# Revit family: Remeha E-HP AW 168 Plus - Rev A
name_source: partatom
category: Mechanical Equipment
units: mm (PartAtom-declared; Revit-internal decimal feet)

## family parameters
Always vertical = Yes
Cut with Voids When Loaded = No
OmniClass Number = 23.75.00.00
OmniClass Title = Climate Control (HVAC)
Part Type = Normal
Room Calculation Point = No
Round Connector Dimension = Use Diameter
Shared = No
Work Plane-Based = No

## types (1)
- Remeha E-HP AW 168 Plus
    6 Monthly = 05-31
    Access Clearance Bottom = 0 mm  [stored 0 ft]
    Access Clearance Front = 2000 mm  [stored 6.56168 ft]
    Access Clearance Left = 3000 mm  [stored 9.84252 ft]
    Access Clearance Rear = 2000 mm  [stored 6.56168 ft]
    Access Clearance Right = 3000 mm  [stored 9.84252 ft]
    Access Clearance Top = 0 mm  [stored 0 ft]
    Annually = 05-31
    BMS Links = Yes
    Bespoke Timeframe = 0
    CE Mark = Yes
    Coefficient of Performance = 5.16
    Colour = IGP Dura Pol (Brand Colour)
    Condensate Drain Size = 0 mm  [stored 0 ft]
    Configuration = Single unit
    Control Options = Modulating
    Control Type = Weather Compensation, 0-10V, Time Control, DHW Control.
    Daily = 0
    Default Elevation = 0 mm  [stored 0 ft]
    Drain Connection Size = 70 mm  [stored 0.229659 ft]
    Drain Connection Type = Threaded
    Embodied Carbon = 0
    ErP Energy Label = 0
    Expected Life = 0
    External Material = Steel
    Features = The Remeha E-HP AW can be used in projects ranging from small light commercial properties to multi-valent energy centres for large commercial buildings
    Finish = Galvanised & Powder Coated
    Flow and Return Connection Size = 65 mm
    Flow and Return Connection Type = Threaded
    Frequency = 50 Hz
    Full Load Current = 121 A
    Fuse Rating = 0 A
    Global Warming Potential of Refrigerant = 1774
    Gross Weight = 2300.00 kg
    Heat Exchanger Material = Stainless Steel
    IP Rating Electrical Enclosure = IP42
    IfcExportAs = IfcHeatExchangerType
    IfcExportType = NOTDEFINED
    Interlocks = Yes
    Life Cycle Analysis = 0
    Mass of Refrigerant = 36.00 kg
    Maximum Air Flow Rate = 0
    Maximum Air Temperature for Cylinder Charging only = 20
    Maximum Air Temperature for Heating only = 20
    Maximum DHW Flow Temperature = 20
    Maximum Heating Operating Pressure = 3200000.0 Pa
    Maximum Heating Output = 151100 W
    Maximum Heating Water Flow Rate = 7.2 L/s
    Maximum Operating Pressure of Refrigerant = 3500000.0 Pa
    Maximum Power Consumption = 32200 W
    Minimum Air Temperature for Heating and Cylinder Charging = -15
    Minimum Heating Operating Pressure = 0.0 Pa
    Minimum Heating Water Flow Rate = 3.6 L/s
    Minimum Operating Pressure of Refrigerant = 0.0 Pa
    Monthly = 0
    Mounting = Floor Standing
    Overall Height = 2268 mm  [stored 7.44094 ft]
    Overall Length = 2280 mm
    Overall Width = 2130 mm
    Product Literature = https://www.remeha.co.uk
    Product Range = E-HP AW 168 Plus
    Quarterly = 0
    Rated Current = 0 A
    Reference Standard = Machine directive 2006/42/EC, Low tension directive 2006/95/EC, EMC directive 2004/108/EC, Pressure Equipment directive 97/23/EWG
    Refrigerant Type = R407C
    Refrigeration Circuit Type = Single Circuit
    Safety Valve Connection Size = 0 mm  [stored 0 ft]
    Seasonal Coefficient of Performance = 4.26
    Seasonal Space Heating Efficiency = 167
    Shape = Rectangular (Horizontal)
    Shipping Weight = 0.00 kg
    Sound Power Level for A7W35 = 67
    Starting Current = 151 A
    Supply Phase = 3
    Type = Monoblock
    Uniclass2015 = Pr_70_60_37_04
    Voltage = 400 V
    Warranty ID = https://mediacdn.pottertoncommercial.co.uk
    Water Content = 0.02 m³
    Weekly = 0

note: [stored X ft] marks values corroborated as IEEE doubles in the binary element streams (Revit-internal decimal feet)

## geometry (parser evidence)
native form markers: Sweep x3
no freeform markers — native parametric forms only
